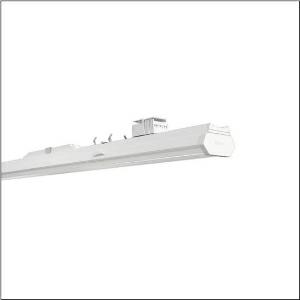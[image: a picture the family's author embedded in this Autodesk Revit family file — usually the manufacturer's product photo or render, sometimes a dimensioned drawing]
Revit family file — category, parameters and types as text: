
# Revit family: licross_r__21_protected_ho_52td12dn4e5m3s_02cf
name_source: partatom
category: Lighting Fixtures
units: mm (PartAtom-declared; Revit-internal decimal feet)

## family parameters
Cut with Voids When Loaded = No
Host = Face
Light Source = No
Part Type = Normal
Room Calculation Point = No
Round Connector Dimension = Use Diameter
Shared = No

## types (1)
- --- (1 x LED, 910 lm, 7.6 W, 4000K)
    Apparent Load = 8 VA
    CIE Flux Codes = 70 91 97 98 100
    Color Rendering = 80
    Color Temperature = 4000K
    Default Elevation = 1800 mm
    Description = Licross® 21 Protected HO, luminaire insert, of sheet steel, galvanised, coil coated, white, length: 1.500mm, width: 90mm, height: 103mm, LED rated luminous flux: 14.690lm, light colour: 840, control gear: DALI 2 (for two DALI lines), with plug, 6-pole, with phase selection, for trunking rail, 14-core, mains connection: 220..240V, AC, 50/60Hz, rated input power: 89W, for trunking rail, 14-core, internal wiring halogen-free, for emergency light function, converter,control gear: single battery element, battery: LiFePO4, 9Ah, primary light control with lens, of plastic, primary optical cover: cover, of PMMA, light emission: direct distribution, primary light characteristic: symmetric, protection rating (complete): IP54, insulation class (complete): insulation class I (protective earthing), certification: CE, UKCA, protection symbol: D if used in an environment with non-conductive dust loads with corresponding accessories, impact resistance: IK06, permissible ambient temperature for indoor applications: +5..+30°C, standard: EN 60598-2-22, LABS conformity tested according to VDMA 24364:2018-05, reducing of maximum allowable ambient temperature of 5°C with ceiling mounting, corresponds to IFS (International Featured Standards) requirements for safety and quality in the food industry, packaging unit: 1 piece
    Height = 92 mm
    Lamp = 1 x LED
    Lamp Light Flux = 910 lm
    Lamp Power = 7.6 W
    Lamp count = 1
    Length = 1500 mm
    Luminous efficacy = 120 lm/W
    Manufacturer = Siteco
    ModVariant = No
    Model = 52TD12DN4E5M3S
    Mounting Place = Ceiling
    Mounting Type = Pendant
    Number of Poles = 1
    OnlyDefault = Yes
    Power Factor = 1
    Product Name = Licross® 21 Protected HO
    Product group = luminaire insert | ceiling pendant
    ProductGroupID = 902
    Protection Class = Protection class I
    Protection Degree = IP 54
    RLX_Detail_Level = 1
    RLX_Emergency_Light_Flux = 0 lm
    RLX_Emergency_Type = 0
    RLX_Emergency_Type_DB = No
    RlxData = <blob elided: 24909 chars, md5=c70e0800>
    Socket = socket
    Standby Power = 0 W
    System Light Flux = 910 lm
    System Power = 8 W
    Type Comments = : emergency light operation: 3 h
    Type Image = l_1256148.jpg
    URL = http://relux.com
    VarID = @adj_132709
    Voltage = 0 V
    Weight = 0.00 kg
    Width = 88 mm

## geometry (parser evidence)
native form markers: Blend x4, Sweep x8
no freeform markers — native parametric forms only
